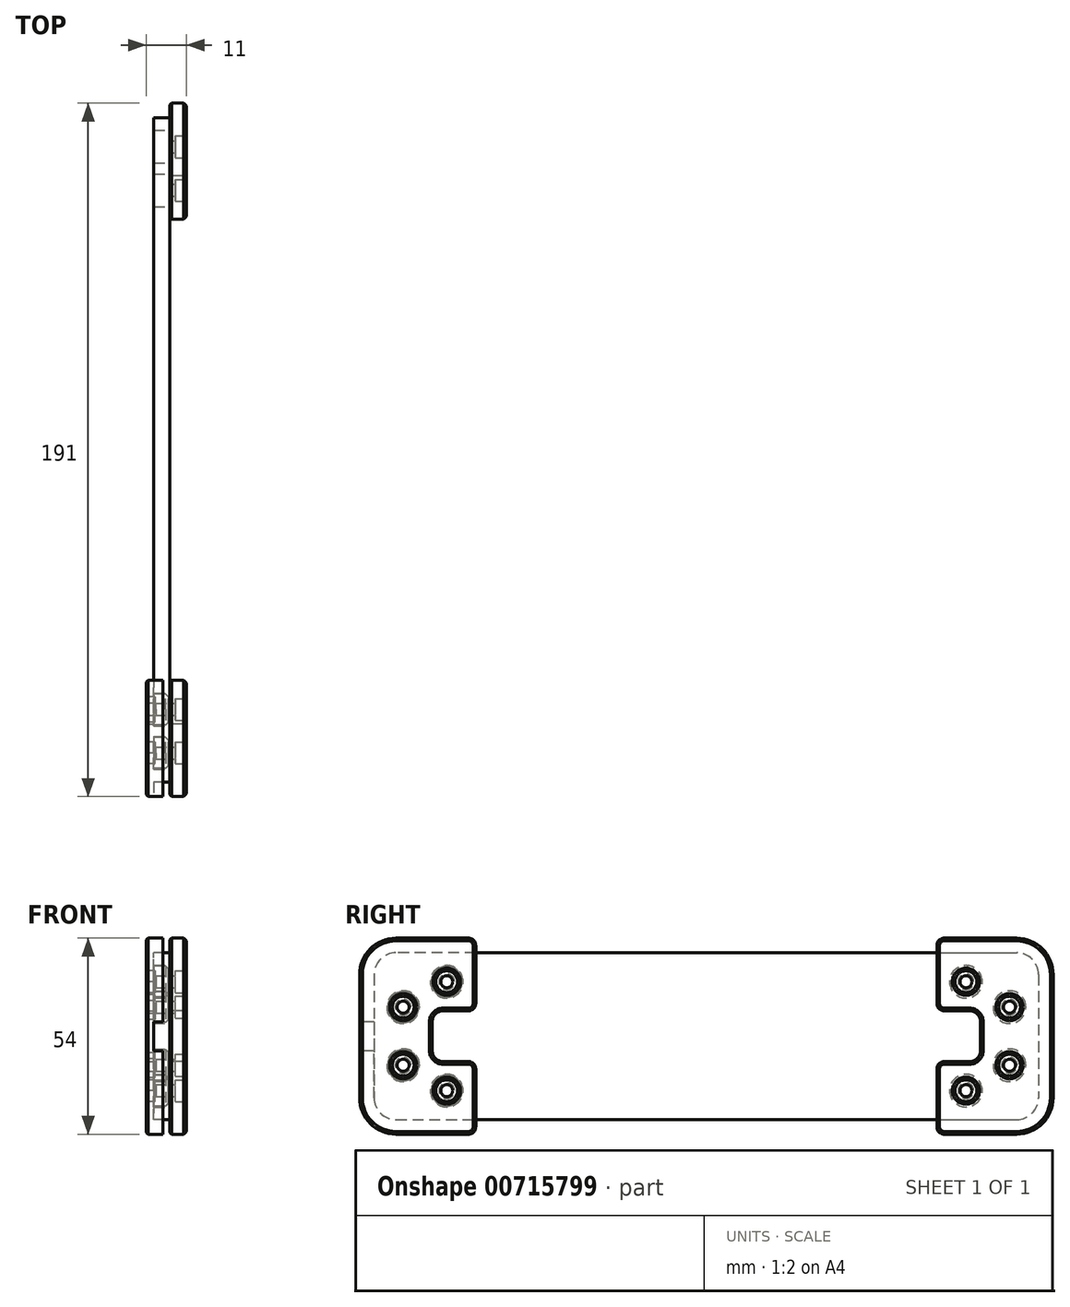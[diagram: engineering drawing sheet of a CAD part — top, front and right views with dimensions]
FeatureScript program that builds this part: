
annotation { "Feature Type Name" : "Feature", "Feature Type Description" : "" }
export const myFeature = defineFeature(function(context is Context, id is Id, definition is map)
    precondition{}
    {
        {
            assignVariable(context, id + "F0", {"name" : "thickness", "anyValue" : 4.5});
        }
        {
            var Q0;
            Q0=qCreatedBy(makeId("Right.planeOp"),FACE);
            var sketch = newSketch(context, id + "F1", { "sketchPlane" : qUnion([Q0])});
            skLineSegment(sketch, "E0.bottom", {"start": v(-85.5, 23) * mm, "end": v(85.5, 23) * mm});
            skLineSegment(sketch, "E0.top", {"start": v(-85.5, -23) * mm, "end": v(85.5, -23) * mm});
            skLineSegment(sketch, "E0.left", {"start": v(-91.5, 17) * mm, "end": v(-91.5, -17) * mm});
            skLineSegment(sketch, "E0.right", {"start": v(91.5, 17) * mm, "end": v(91.5, -17) * mm});
            skPoint(sketch, "E0.middle", {"position": v(0, 0) * mm});
            skPoint(sketch, "E1.visualSharp", {"position": v(-91.5, 23) * mm});
            skArc(sketch, "E1.filletArc", {"start": v(-85.5, 23) * mm, "mid": v(-89.74, 21.24) * mm, "end": v(-91.5, 17) * mm});
            skPoint(sketch, "E2.visualSharp", {"position": v(-91.5, -23) * mm});
            skArc(sketch, "E2.filletArc", {"start": v(-91.5, -17) * mm, "mid": v(-89.74, -21.24) * mm, "end": v(-85.5, -23) * mm});
            skPoint(sketch, "E3.visualSharp", {"position": v(91.5, -23) * mm});
            skArc(sketch, "E3.filletArc", {"start": v(85.5, -23) * mm, "mid": v(89.74, -21.24) * mm, "end": v(91.5, -17) * mm});
            skPoint(sketch, "E4.visualSharp", {"position": v(91.5, 23) * mm});
            skArc(sketch, "E4.filletArc", {"start": v(91.5, 17) * mm, "mid": v(89.74, 21.24) * mm, "end": v(85.5, 23) * mm});
            skSolve(sketch);
        }
        {
            var Q0;
            Q0 = qSketchRegion(id + "F1", true);
            extrude(context, id + "F2", {"entities" : qUnion([Q0]), "endBound" : BoundingType.SYMMETRIC, "depth" : (getVariable(context, 'thickness')) * mm, "offsetDistance" : 25 * mm});
        }
        {
            var Q0;
            Q0=qCreatedBy(makeId("Right.planeOp"),FACE);
            var sketch = newSketch(context, id + "F3", { "sketchPlane" : qUnion([Q0])});
            skCircle(sketch, "E5", {"center": v(-83.5, -8) * mm, "radius": 4.5 * mm});
            skCircle(sketch, "E6", {"center": v(-71.5, -15) * mm, "radius": 4.5 * mm});
            skCircle(sketch, "E7.MirrorC", {"center": v(83.5, -8) * mm, "radius": 4.5 * mm});
            skCircle(sketch, "E8.MirrorC", {"center": v(71.5, -15) * mm, "radius": 4.5 * mm});
            skCircle(sketch, "E9.MirrorC", {"center": v(83.5, 8) * mm, "radius": 4.5 * mm});
            skCircle(sketch, "E10.MirrorC", {"center": v(71.5, 15) * mm, "radius": 4.5 * mm});
            skCircle(sketch, "E11.MirrorC", {"center": v(-71.5, 15) * mm, "radius": 4.5 * mm});
            skCircle(sketch, "E12.MirrorC", {"center": v(-83.5, 8) * mm, "radius": 4.5 * mm});
            skSolve(sketch);
        }
        {
            var Q0;
            Q0 = qSketchRegion(id + "F3", true);
            extrude(context, id + "F4", {"entities" : qUnion([Q0]), "operationType" : NewBodyOperationType.REMOVE, "endBound" : BoundingType.SYMMETRIC, "oppositeDirection" : true, "depth" : 5 * mm, "offsetDistance" : 25 * mm});
        }
        {
            var Q0;
            Q0=makeQuery(id+"F2.opExtrude","CAP_FACE",FACE,{"disambiguationData":[OSD([sQuery(id+"F1.wireOp",EDGE,"E0.bottom"),sQuery(id+"F1.wireOp",EDGE,"E0.top"),sQuery(id+"F1.wireOp",EDGE,"E0.left"),sQuery(id+"F1.wireOp",EDGE,"E0.right"),sQuery(id+"F1.wireOp",EDGE,"E1.filletArc"),sQuery(id+"F1.wireOp",EDGE,"E2.filletArc"),sQuery(id+"F1.wireOp",EDGE,"E3.filletArc"),sQuery(id+"F1.wireOp",EDGE,"E4.filletArc")])],"isStart":false});
            var sketch = newSketch(context, id + "F5", { "sketchPlane" : qUnion([Q0])});
            skLineSegment(sketch, "E13", {"start": v(-75.5, 4) * mm, "end": v(-75.5, -4) * mm});
            skLineSegment(sketch, "E14", {"start": v(-72.5, -7) * mm, "end": v(-63.5, -7) * mm});
            skLineSegment(sketch, "E15", {"start": v(-63.5, -7) * mm, "end": v(-63.5, -27) * mm});
            skLineSegment(sketch, "E16", {"start": v(-63.5, -27) * mm, "end": v(-85.5, -27) * mm});
            skLineSegment(sketch, "E17", {"start": v(-95.5, -17) * mm, "end": v(-95.5, 17) * mm});
            skPoint(sketch, "E18.visualSharp", {"position": v(-75.5, -7) * mm});
            skArc(sketch, "E18.filletArc", {"start": v(-75.5, -4) * mm, "mid": v(-74.62, -6.12) * mm, "end": v(-72.5, -7) * mm});
            skPoint(sketch, "E19.visualSharp", {"position": v(-95.5, -27) * mm});
            skArc(sketch, "E19.filletArc", {"start": v(-95.5, -17) * mm, "mid": v(-92.57, -24.07) * mm, "end": v(-85.5, -27) * mm});
            skLineSegment(sketch, "E20", {"start": v(-83.5, -8) * mm, "end": v(-83.5, 0) * mm, "construction": true});
            skLineSegment(sketch, "E21", {"start": v(-71.5, -15) * mm, "end": v(-63.5, -15) * mm, "construction": true});
            skLineSegment(sketch, "E22", {"start": v(-83.5, -1.98) * mm, "end": v(-75.5, -1.98) * mm, "construction": true});
            skPoint(sketch, "E23.MirrorP", {"position": v(-95.5, 27) * mm});
            skLineSegment(sketch, "E24.MirrorCS", {"start": v(-63.5, 27) * mm, "end": v(-85.5, 27) * mm});
            skLineSegment(sketch, "E25.MirrorCS", {"start": v(-71.5, 15) * mm, "end": v(-63.5, 15) * mm, "construction": true});
            skLineSegment(sketch, "E26.MirrorCS", {"start": v(-83.5, 8) * mm, "end": v(-83.5, 0) * mm, "construction": true});
            skPoint(sketch, "E27.MirrorP", {"position": v(-75.5, 7) * mm});
            skLineSegment(sketch, "E28.MirrorCS", {"start": v(-63.5, 7) * mm, "end": v(-63.5, 27) * mm});
            skLineSegment(sketch, "E29.MirrorCS", {"start": v(-72.5, 7) * mm, "end": v(-63.5, 7) * mm});
            skArc(sketch, "E30.MirrorCS", {"start": v(-75.5, 4) * mm, "mid": v(-74.62, 6.12) * mm, "end": v(-72.5, 7) * mm});
            skArc(sketch, "E31.MirrorCS", {"start": v(-95.5, 17) * mm, "mid": v(-92.57, 24.07) * mm, "end": v(-85.5, 27) * mm});
            skSolve(sketch);
        }
        {
            var Q0;
            Q0 = qSketchRegion(id + "F5", true);
            extrude(context, id + "F6", {"entities" : qUnion([Q0]), "depth" : 4.5 * mm, "offsetDistance" : 25 * mm});
        }
        {
            var Q0;
            Q0=makeQuery(id+"F6.opExtrude","SWEPT_EDGE",EDGE,{"disambiguationData":[OSD([sQuery(id+"F5.wireOp",EDGE,"E17"),sQuery(id+"F5.wireOp",EDGE,"RyQupdBu-5okV-t9er-J7do-R5SVAbqqGuGU")])]});
            var Q1;
            Q1=makeQuery(id+"F6.opExtrude","SWEPT_EDGE",EDGE,{"disambiguationData":[OSD([sQuery(id+"F5.wireOp",EDGE,"E13"),sQuery(id+"F5.wireOp",EDGE,"RyQupdBu-5okV-t9er-J7do-R5SVAbqqGuGU")])]});
            var Q2;
            Q2=makeQuery(id+"F6.opExtrude","SWEPT_EDGE",EDGE,{"disambiguationData":[OSD([sQuery(id+"F5.wireOp",EDGE,"E14"),sQuery(id+"F5.wireOp",EDGE,"E15")])]});
            var Q3;
            Q3=makeQuery(id+"F6.opExtrude","SWEPT_EDGE",EDGE,{"disambiguationData":[OSD([sQuery(id+"F5.wireOp",EDGE,"E15"),sQuery(id+"F5.wireOp",EDGE,"E16")])]});
            var Q4;
            Q4=makeQuery(id+"F6.opExtrude","SWEPT_EDGE",EDGE,{"disambiguationData":[OSD([sQuery(id+"F5.wireOp",EDGE,"E28.MirrorCS"),sQuery(id+"F5.wireOp",EDGE,"E29.MirrorCS")])]});
            var Q5;
            Q5=makeQuery(id+"F6.opExtrude","SWEPT_EDGE",EDGE,{"disambiguationData":[OSD([sQuery(id+"F5.wireOp",EDGE,"E24.MirrorCS"),sQuery(id+"F5.wireOp",EDGE,"E28.MirrorCS")])]});
            fillet(context, id + "F7", {"entities" : qUnion([Q0, Q1, Q2, Q3, Q4, Q5]), "radius" : 2 * mm, "tangentPropagation" : true, "allowEdgeOverflow" : false});
        }
        {
            var Q0;
            Q0=makeQuery(id+"F2.opExtrude","CAP_FACE",FACE,{"disambiguationData":[OSD([sQuery(id+"F1.wireOp",EDGE,"E0.bottom"),sQuery(id+"F1.wireOp",EDGE,"E0.top"),sQuery(id+"F1.wireOp",EDGE,"E0.left"),sQuery(id+"F1.wireOp",EDGE,"E0.right"),sQuery(id+"F1.wireOp",EDGE,"E1.filletArc"),sQuery(id+"F1.wireOp",EDGE,"E2.filletArc"),sQuery(id+"F1.wireOp",EDGE,"E3.filletArc"),sQuery(id+"F1.wireOp",EDGE,"E4.filletArc")])],"isStart":true});
            var sketch = newSketch(context, id + "F8", { "sketchPlane" : qUnion([Q0])});
            skLineSegment(sketch, "E32.0", {"start": v(72.5, -7) * mm, "end": v(63.5, -7) * mm});
            skLineSegment(sketch, "E32.1", {"start": v(75.5, 0) * mm, "end": v(75.5, -4) * mm});
            skLineSegment(sketch, "E32.2", {"start": v(63.5, -27) * mm, "end": v(85.5, -27) * mm});
            skArc(sketch, "E32.3", {"start": v(95.5, -17) * mm, "mid": v(92.57, -24.07) * mm, "end": v(85.5, -27) * mm});
            skLineSegment(sketch, "E32.4", {"start": v(95.5, -17) * mm, "end": v(95.5, 0) * mm});
            skLineSegment(sketch, "E32.5", {"start": v(63.5, -7) * mm, "end": v(63.5, -27) * mm});
            skPoint(sketch, "E33.visualSharp", {"position": v(75.5, -7) * mm});
            skArc(sketch, "E33.filletArc", {"start": v(72.5, -7) * mm, "mid": v(74.62, -6.12) * mm, "end": v(75.5, -4) * mm});
            skArc(sketch, "E34.MirrorCS", {"start": v(72.5, 7) * mm, "mid": v(74.62, 6.12) * mm, "end": v(75.5, 4) * mm});
            skLineSegment(sketch, "E35.MirrorCS", {"start": v(72.5, 7) * mm, "end": v(63.5, 7) * mm});
            skLineSegment(sketch, "E36.MirrorCS", {"start": v(63.5, 27) * mm, "end": v(85.5, 27) * mm});
            skLineSegment(sketch, "E37.MirrorCS", {"start": v(63.5, 7) * mm, "end": v(63.5, 27) * mm});
            skLineSegment(sketch, "E38.MirrorCS", {"start": v(75.5, 0) * mm, "end": v(75.5, 4) * mm});
            skPoint(sketch, "E39.MirrorP", {"position": v(75.5, 7) * mm});
            skArc(sketch, "E40.MirrorCS", {"start": v(95.5, 17) * mm, "mid": v(92.57, 24.07) * mm, "end": v(85.5, 27) * mm});
            skLineSegment(sketch, "E41.MirrorCS", {"start": v(95.5, 17) * mm, "end": v(95.5, 0) * mm});
            skSolve(sketch);
        }
        {
            var Q0;
            Q0 = qSketchRegion(id + "F8", true);
            extrude(context, id + "F9", {"entities" : qUnion([Q0]), "depth" : 2 * mm, "offsetDistance" : 25 * mm});
        }
        {
            var Q0;
            Q0=makeQuery(id+"F9.opExtrude","CAP_FACE",FACE,{"disambiguationData":[OSD([sQuery(id+"F8.wireOp",EDGE,"E32.0"),sQuery(id+"F8.wireOp",EDGE,"E32.1"),sQuery(id+"F8.wireOp",EDGE,"E32.2"),sQuery(id+"F8.wireOp",EDGE,"E32.3"),sQuery(id+"F8.wireOp",EDGE,"E32.4"),sQuery(id+"F8.wireOp",EDGE,"E32.5"),sQuery(id+"F8.wireOp",EDGE,"E32.6"),sQuery(id+"F8.wireOp",EDGE,"E33.filletArc")])],"isStart":true});
            var sketch = newSketch(context, id + "F10", { "sketchPlane" : qUnion([Q0])});
            skLineSegment(sketch, "E42", {"start": v(-95.5, -4) * mm, "end": v(-95.5, -17) * mm});
            skLineSegment(sketch, "E43", {"start": v(-85.5, -27) * mm, "end": v(-63.5, -27) * mm});
            skLineSegment(sketch, "E44", {"start": v(-63.5, -27) * mm, "end": v(-63.5, -23) * mm});
            skLineSegment(sketch, "E45", {"start": v(-63.5, -23) * mm, "end": v(-85.5, -23) * mm});
            skLineSegment(sketch, "E46", {"start": v(-91.5, -17) * mm, "end": v(-91.5, -4) * mm});
            skLineSegment(sketch, "E47", {"start": v(-91.5, -4) * mm, "end": v(-95.5, -4) * mm});
            skPoint(sketch, "E48.visualSharp", {"position": v(-91.5, -23) * mm});
            skArc(sketch, "E48.filletArc", {"start": v(-91.5, -17) * mm, "mid": v(-89.74, -21.24) * mm, "end": v(-85.5, -23) * mm});
            skPoint(sketch, "E49.visualSharp", {"position": v(-95.5, -27) * mm});
            skArc(sketch, "E49.filletArc", {"start": v(-95.5, -17) * mm, "mid": v(-92.57, -24.07) * mm, "end": v(-85.5, -27) * mm});
            skLineSegment(sketch, "E50.MirrorCS", {"start": v(-85.5, 27) * mm, "end": v(-63.5, 27) * mm});
            skPoint(sketch, "E51.MirrorP", {"position": v(-95.5, 27) * mm});
            skLineSegment(sketch, "E52.MirrorCS", {"start": v(-91.5, 17) * mm, "end": v(-91.5, 4) * mm});
            skPoint(sketch, "E53.MirrorP", {"position": v(-91.5, 23) * mm});
            skArc(sketch, "E54.MirrorCS", {"start": v(-95.5, 17) * mm, "mid": v(-92.57, 24.07) * mm, "end": v(-85.5, 27) * mm});
            skLineSegment(sketch, "E55.MirrorCS", {"start": v(-95.5, 4) * mm, "end": v(-95.5, 17) * mm});
            skLineSegment(sketch, "E56.MirrorCS", {"start": v(-91.5, 4) * mm, "end": v(-95.5, 4) * mm});
            skLineSegment(sketch, "E57.MirrorCS", {"start": v(-63.5, 23) * mm, "end": v(-85.5, 23) * mm});
            skLineSegment(sketch, "E58.MirrorCS", {"start": v(-63.5, 27) * mm, "end": v(-63.5, 23) * mm});
            skArc(sketch, "E59.MirrorCS", {"start": v(-91.5, 17) * mm, "mid": v(-89.74, 21.24) * mm, "end": v(-85.5, 23) * mm});
            skSolve(sketch);
        }
        {
            var Q0;
            Q0 = qSketchRegion(id + "F10", true);
            extrude(context, id + "F11", {"entities" : qUnion([Q0]), "operationType" : NewBodyOperationType.ADD, "depth" : 2.5 * mm, "offsetDistance" : 25 * mm});
        }
        {
            var Q0;
            Q0=makeQuery(id+"F9.opExtrude","SWEPT_EDGE",EDGE,{"disambiguationData":[OSD([sQuery(id+"F8.wireOp",EDGE,"E32.2"),sQuery(id+"F8.wireOp",EDGE,"E32.5")])]});
            var Q1;
            Q1=makeQuery(id+"F9.opExtrude","SWEPT_EDGE",EDGE,{"disambiguationData":[OSD([sQuery(id+"F8.wireOp",EDGE,"E32.0"),sQuery(id+"F8.wireOp",EDGE,"E32.5")])]});
            var Q2;
            Q2=makeQuery(id+"F9.opExtrude","SWEPT_EDGE",EDGE,{"disambiguationData":[OSD([sQuery(id+"F8.wireOp",EDGE,"E32.1"),sQuery(id+"F8.wireOp",EDGE,"E32.6")])]});
            var Q3;
            Q3=makeQuery(id+"F9.opExtrude","SWEPT_EDGE",EDGE,{"disambiguationData":[OSD([sQuery(id+"F8.wireOp",EDGE,"E32.4"),sQuery(id+"F8.wireOp",EDGE,"E32.6")])]});
            var Q4;
            Q4=makeQuery(id+"F11.boolean.opBoolean","MERGE",EDGE,{"derivedFrom":[makeQuery(id+"F9.opExtrude","SWEPT_EDGE",EDGE,{"disambiguationData":[OSD([sQuery(id+"F8.wireOp",EDGE,"E36.MirrorCS"),sQuery(id+"F8.wireOp",EDGE,"E37.MirrorCS")])]}),makeQuery(id+"F11.opExtrude","SWEPT_EDGE",EDGE,{"disambiguationData":[OSD([sQuery(id+"F10.wireOp",EDGE,"E50.MirrorCS"),sQuery(id+"F10.wireOp",EDGE,"E58.MirrorCS")])]})]});
            var Q5;
            Q5=makeQuery(id+"F9.opExtrude","SWEPT_EDGE",EDGE,{"disambiguationData":[OSD([sQuery(id+"F8.wireOp",EDGE,"E35.MirrorCS"),sQuery(id+"F8.wireOp",EDGE,"E37.MirrorCS")])]});
            fillet(context, id + "F12", {"entities" : qUnion([Q0, Q1, Q2, Q3, Q4, Q5]), "radius" : 2 * mm, "tangentPropagation" : true, "allowEdgeOverflow" : false});
        }
        {
            var Q0;
            Q0=makeQuery(id+"F9.opExtrude","CAP_FACE",FACE,{"disambiguationData":[OSD([sQuery(id+"F8.wireOp",EDGE,"E32.0"),sQuery(id+"F8.wireOp",EDGE,"E32.1"),sQuery(id+"F8.wireOp",EDGE,"E32.2"),sQuery(id+"F8.wireOp",EDGE,"E32.3"),sQuery(id+"F8.wireOp",EDGE,"E32.4"),sQuery(id+"F8.wireOp",EDGE,"E32.5"),sQuery(id+"F8.wireOp",EDGE,"E32.6"),sQuery(id+"F8.wireOp",EDGE,"E33.filletArc")])],"isStart":true});
            var sketch = newSketch(context, id + "F13", { "sketchPlane" : qUnion([Q0])});
            skCircle(sketch, "E60", {"center": v(-71.5, -15) * mm, "radius": 4.25 * mm});
            skCircle(sketch, "E61", {"center": v(-83.5, -8) * mm, "radius": 4.25 * mm});
            skCircle(sketch, "E62.MirrorC", {"center": v(-83.5, 8) * mm, "radius": 4.25 * mm});
            skCircle(sketch, "E63.MirrorC", {"center": v(-71.5, 15) * mm, "radius": 4.25 * mm});
            skSolve(sketch);
        }
        {
            var Q0;
            Q0 = qSketchRegion(id + "F13", true);
            extrude(context, id + "F14", {"entities" : qUnion([Q0]), "operationType" : NewBodyOperationType.ADD, "depth" : 4 * mm, "offsetDistance" : 25 * mm});
        }
        {
            var Q0;
            Q0=makeQuery(id+"F14.opExtrude","CAP_FACE",FACE,{"disambiguationData":[OSD([sQuery(id+"F13.wireOp",EDGE,"E61")])],"isStart":false});
            var sketch = newSketch(context, id + "F15", { "sketchPlane" : qUnion([Q0])});
            skCircle(sketch, "E64", {"center": v(-71.5, -15) * mm, "radius": 1.65 * mm});
            skCircle(sketch, "E65", {"center": v(-83.5, -8) * mm, "radius": 1.65 * mm});
            skCircle(sketch, "E66.MirrorC", {"center": v(-71.5, 15) * mm, "radius": 1.65 * mm});
            skCircle(sketch, "E67.MirrorC", {"center": v(-83.5, 8) * mm, "radius": 1.65 * mm});
            skSolve(sketch);
        }
        {
            var Q0;
            Q0 = qSketchRegion(id + "F15", true);
            extrude(context, id + "F16", {"entities" : qUnion([Q0]), "operationType" : NewBodyOperationType.REMOVE, "endBound" : BoundingType.THROUGH_ALL, "oppositeDirection" : true, "depth" : 25 * mm, "offsetDistance" : 25 * mm});
        }
        {
            var Q0;
            Q0=makeQuery(id+"F9.opExtrude","CAP_FACE",FACE,{"disambiguationData":[OSD([sQuery(id+"F8.wireOp",EDGE,"E32.0"),sQuery(id+"F8.wireOp",EDGE,"E32.1"),sQuery(id+"F8.wireOp",EDGE,"E32.2"),sQuery(id+"F8.wireOp",EDGE,"E32.3"),sQuery(id+"F8.wireOp",EDGE,"E32.4"),sQuery(id+"F8.wireOp",EDGE,"E32.5"),sQuery(id+"F8.wireOp",EDGE,"E32.6"),sQuery(id+"F8.wireOp",EDGE,"E33.filletArc")])],"isStart":false});
            var sketch = newSketch(context, id + "F17", { "sketchPlane" : qUnion([Q0])});
            skCircle(sketch, "E68.cCircle", {"center": v(71.5, -15) * mm, "radius": 3.46 * mm, "construction": true});
            skLineSegment(sketch, "E68.0", {"start": v(69.77, -12) * mm, "end": v(73.23, -12) * mm});
            skLineSegment(sketch, "E68.1", {"start": v(73.23, -12) * mm, "end": v(74.96, -15) * mm});
            skLineSegment(sketch, "E68.2", {"start": v(74.96, -15) * mm, "end": v(73.23, -18) * mm});
            skLineSegment(sketch, "E68.3", {"start": v(73.23, -18) * mm, "end": v(69.77, -18) * mm});
            skLineSegment(sketch, "E68.4", {"start": v(69.77, -18) * mm, "end": v(68.04, -15) * mm});
            skLineSegment(sketch, "E68.5", {"start": v(68.04, -15) * mm, "end": v(69.77, -12) * mm});
            skCircle(sketch, "E69.cCircle", {"center": v(83.5, -8) * mm, "radius": 3.46 * mm, "construction": true});
            skLineSegment(sketch, "E69.0", {"start": v(80.5, -6.27) * mm, "end": v(83.5, -4.54) * mm});
            skLineSegment(sketch, "E69.1", {"start": v(83.5, -4.54) * mm, "end": v(86.5, -6.27) * mm});
            skLineSegment(sketch, "E69.2", {"start": v(86.5, -6.27) * mm, "end": v(86.5, -9.73) * mm});
            skLineSegment(sketch, "E69.3", {"start": v(86.5, -9.73) * mm, "end": v(83.5, -11.46) * mm});
            skLineSegment(sketch, "E69.4", {"start": v(83.5, -11.46) * mm, "end": v(80.5, -9.73) * mm});
            skLineSegment(sketch, "E69.5", {"start": v(80.5, -9.73) * mm, "end": v(80.5, -6.27) * mm});
            skLineSegment(sketch, "E70.MirrorCS", {"start": v(68.04, 15) * mm, "end": v(69.77, 12) * mm});
            skLineSegment(sketch, "E71.MirrorCS", {"start": v(69.77, 18) * mm, "end": v(68.04, 15) * mm});
            skLineSegment(sketch, "E72.MirrorCS", {"start": v(69.77, 12) * mm, "end": v(73.23, 12) * mm});
            skLineSegment(sketch, "E73.MirrorCS", {"start": v(74.96, 15) * mm, "end": v(73.23, 18) * mm});
            skLineSegment(sketch, "E74.MirrorCS", {"start": v(73.23, 18) * mm, "end": v(69.77, 18) * mm});
            skLineSegment(sketch, "E75.MirrorCS", {"start": v(73.23, 12) * mm, "end": v(74.96, 15) * mm});
            skLineSegment(sketch, "E76.MirrorCS", {"start": v(83.5, 4.54) * mm, "end": v(86.5, 6.27) * mm});
            skLineSegment(sketch, "E77.MirrorCS", {"start": v(86.5, 9.73) * mm, "end": v(83.5, 11.46) * mm});
            skCircle(sketch, "E78.MirrorC", {"center": v(71.5, 15) * mm, "radius": 3.46 * mm, "construction": true});
            skLineSegment(sketch, "E79.MirrorCS", {"start": v(86.5, 6.27) * mm, "end": v(86.5, 9.73) * mm});
            skCircle(sketch, "E80.MirrorC", {"center": v(83.5, 8) * mm, "radius": 3.46 * mm, "construction": true});
            skLineSegment(sketch, "E81.MirrorCS", {"start": v(80.5, 9.73) * mm, "end": v(80.5, 6.27) * mm});
            skLineSegment(sketch, "E82.MirrorCS", {"start": v(80.5, 6.27) * mm, "end": v(83.5, 4.54) * mm});
            skLineSegment(sketch, "E83.MirrorCS", {"start": v(83.5, 11.46) * mm, "end": v(80.5, 9.73) * mm});
            skSolve(sketch);
        }
        {
            var Q0;
            Q0 = qSketchRegion(id + "F17", true);
            extrude(context, id + "F18", {"entities" : qUnion([Q0]), "operationType" : NewBodyOperationType.REMOVE, "oppositeDirection" : true, "depth" : 2.4 * mm, "offsetDistance" : 25 * mm});
        }
        {
            var Q0;
            Q0=makeQuery(id+"F14.opExtrude","CAP_EDGE",EDGE,{"disambiguationData":[OSD([sQuery(id+"F13.wireOp",EDGE,"99nuNubE-fCBx-eOUg-4Eev-Zh7OqMbQXb6X")])],"isStart":false});
            var Q1;
            Q1=makeQuery(id+"F14.opExtrude","CAP_EDGE",EDGE,{"disambiguationData":[OSD([sQuery(id+"F13.wireOp",EDGE,"E60")])],"isStart":false});
            var Q2;
            Q2=makeQuery(id+"F14.opExtrude","CAP_EDGE",EDGE,{"disambiguationData":[OSD([sQuery(id+"F13.wireOp",EDGE,"E61")])],"isStart":false});
            var Q3;
            Q3=makeQuery(id+"F14.opExtrude","CAP_EDGE",EDGE,{"disambiguationData":[OSD([sQuery(id+"F13.wireOp",EDGE,"E62.MirrorC")])],"isStart":false});
            var Q4;
            Q4=makeQuery(id+"F14.opExtrude","CAP_EDGE",EDGE,{"disambiguationData":[OSD([sQuery(id+"F13.wireOp",EDGE,"E63.MirrorC")])],"isStart":false});
            chamfer(context, id + "F19", {"entities" : qUnion([Q0, Q1, Q2, Q3, Q4]), "width" : .75 * mm, "tangentPropagation" : true});
        }
        {
            var Q0;
            Q0=makeQuery(id+"F9.opExtrude","CAP_FACE",FACE,{"disambiguationData":[OSD([sQuery(id+"F8.wireOp",EDGE,"E32.0"),sQuery(id+"F8.wireOp",EDGE,"E32.1"),sQuery(id+"F8.wireOp",EDGE,"E32.2"),sQuery(id+"F8.wireOp",EDGE,"E32.3"),sQuery(id+"F8.wireOp",EDGE,"E32.4"),sQuery(id+"F8.wireOp",EDGE,"E32.5"),sQuery(id+"F8.wireOp",EDGE,"E32.6"),sQuery(id+"F8.wireOp",EDGE,"E33.filletArc")])],"isStart":false});
            chamfer(context, id + "F20", {"entities" : qUnion([Q0]), "width" : .5 * mm, "tangentPropagation" : true});
        }
        {
            var Q0;
            Q0=makeQuery(id+"F6.opExtrude","CAP_FACE",FACE,{"disambiguationData":[OSD([sQuery(id+"F5.wireOp",EDGE,"E13"),sQuery(id+"F5.wireOp",EDGE,"E14"),sQuery(id+"F5.wireOp",EDGE,"E15"),sQuery(id+"F5.wireOp",EDGE,"E16"),sQuery(id+"F5.wireOp",EDGE,"E17"),sQuery(id+"F5.wireOp",EDGE,"RyQupdBu-5okV-t9er-J7do-R5SVAbqqGuGU"),sQuery(id+"F5.wireOp",EDGE,"E18.filletArc"),sQuery(id+"F5.wireOp",EDGE,"E19.filletArc")])],"isStart":false});
            var sketch = newSketch(context, id + "F21", { "sketchPlane" : qUnion([Q0])});
            skCircle(sketch, "E84", {"center": v(-71.5, -15) * mm, "radius": 3 * mm});
            skCircle(sketch, "E85", {"center": v(-83.5, -8) * mm, "radius": 3 * mm});
            skCircle(sketch, "E86.MirrorC", {"center": v(-83.5, 8) * mm, "radius": 3 * mm});
            skCircle(sketch, "E87.MirrorC", {"center": v(-71.5, 15) * mm, "radius": 3 * mm});
            skSolve(sketch);
        }
        {
            var Q0;
            Q0 = qSketchRegion(id + "F21", true);
            extrude(context, id + "F22", {"entities" : qUnion([Q0]), "operationType" : NewBodyOperationType.REMOVE, "oppositeDirection" : true, "depth" : 3 * mm, "offsetDistance" : 25 * mm});
        }
        {
            var Q0;
            Q0=makeQuery(id+"F22.boolean.opBoolean","COPY",FACE,{"derivedFrom":makeQuery(id+"F22.opExtrude","CAP_FACE",FACE,{"disambiguationData":[OSD([sQuery(id+"F21.wireOp",EDGE,"E85")])],"isStart":false})});
            var sketch = newSketch(context, id + "F23", { "sketchPlane" : qUnion([Q0])});
            skCircle(sketch, "E88", {"center": v(-83.5, -8) * mm, "radius": 1.65 * mm});
            skCircle(sketch, "E89", {"center": v(-71.5, -15) * mm, "radius": 1.65 * mm});
            skCircle(sketch, "E90.MirrorC", {"center": v(-71.5, 15) * mm, "radius": 1.65 * mm});
            skCircle(sketch, "E91.MirrorC", {"center": v(-83.5, 8) * mm, "radius": 1.65 * mm});
            skSolve(sketch);
        }
        {
            var Q0;
            Q0 = qSketchRegion(id + "F23", true);
            extrude(context, id + "F24", {"entities" : qUnion([Q0]), "operationType" : NewBodyOperationType.REMOVE, "endBound" : BoundingType.THROUGH_ALL, "oppositeDirection" : true, "depth" : 25 * mm, "offsetDistance" : 25 * mm});
        }
        {
            var Q0;
            Q0=makeQuery(id+"F6.opExtrude","CAP_FACE",FACE,{"disambiguationData":[OSD([sQuery(id+"F5.wireOp",EDGE,"E13"),sQuery(id+"F5.wireOp",EDGE,"E14"),sQuery(id+"F5.wireOp",EDGE,"E15"),sQuery(id+"F5.wireOp",EDGE,"E16"),sQuery(id+"F5.wireOp",EDGE,"E17"),sQuery(id+"F5.wireOp",EDGE,"RyQupdBu-5okV-t9er-J7do-R5SVAbqqGuGU"),sQuery(id+"F5.wireOp",EDGE,"E18.filletArc"),sQuery(id+"F5.wireOp",EDGE,"E19.filletArc")])],"isStart":false});
            chamfer(context, id + "F25", {"entities" : qUnion([Q0]), "width" : .75 * mm, "tangentPropagation" : true});
        }
        {
            var Q0;
            Q0=makeQuery(id+"F6.opExtrude","CAP_FACE",FACE,{"disambiguationData":[OSD([sQuery(id+"F5.wireOp",EDGE,"E13"),sQuery(id+"F5.wireOp",EDGE,"E14"),sQuery(id+"F5.wireOp",EDGE,"E15"),sQuery(id+"F5.wireOp",EDGE,"E16"),sQuery(id+"F5.wireOp",EDGE,"E17"),sQuery(id+"F5.wireOp",EDGE,"RyQupdBu-5okV-t9er-J7do-R5SVAbqqGuGU"),sQuery(id+"F5.wireOp",EDGE,"E18.filletArc"),sQuery(id+"F5.wireOp",EDGE,"E19.filletArc")])],"isStart":true});
            chamfer(context, id + "F26", {"entities" : qUnion([Q0]), "width" : .5 * mm, "tangentPropagation" : true});
        }
        {
            var Q0;
            Q0=makeQuery(id+"F18.boolean.opBoolean","COPY",FACE,{"derivedFrom":makeQuery(id+"F18.opExtrude","CAP_FACE",FACE,{"disambiguationData":[OSD([sQuery(id+"F17.wireOp",EDGE,"E69.0"),sQuery(id+"F17.wireOp",EDGE,"E69.1"),sQuery(id+"F17.wireOp",EDGE,"E69.2"),sQuery(id+"F17.wireOp",EDGE,"E69.3"),sQuery(id+"F17.wireOp",EDGE,"E69.4"),sQuery(id+"F17.wireOp",EDGE,"E69.5")])],"isStart":false})});
            var sketch = newSketch(context, id + "F27", { "sketchPlane" : qUnion([Q0])});
            skCircle(sketch, "E92", {"center": v(71.5, 15) * mm, "radius": 1.65 * mm});
            skCircle(sketch, "E93", {"center": v(83.5, 8) * mm, "radius": 1.65 * mm});
            skCircle(sketch, "E94", {"center": v(83.5, -8) * mm, "radius": 1.65 * mm});
            skCircle(sketch, "E95", {"center": v(71.5, -15) * mm, "radius": 1.65 * mm});
            skSolve(sketch);
        }
        {
            var Q0;
            Q0 = qSketchRegion(id + "F27", true);
            extrude(context, id + "F28", {"entities" : qUnion([Q0]), "operationType" : NewBodyOperationType.ADD, "oppositeDirection" : true, "depth" : .2 * mm, "offsetDistance" : 25 * mm});
        }
        {
            var Q0;
            Q0=makeQuery(id+"F6.opExtrude","SWEPT_BODY",BODY,{"disambiguationData":[OSD([sQuery(id+"F5.wireOp",EDGE,"E13"),sQuery(id+"F5.wireOp",EDGE,"E14"),sQuery(id+"F5.wireOp",EDGE,"E15"),sQuery(id+"F5.wireOp",EDGE,"E16"),sQuery(id+"F5.wireOp",EDGE,"E17"),sQuery(id+"F5.wireOp",EDGE,"RyQupdBu-5okV-t9er-J7do-R5SVAbqqGuGU"),sQuery(id+"F5.wireOp",EDGE,"E18.filletArc"),sQuery(id+"F5.wireOp",EDGE,"E19.filletArc")])]});
            var Q1;
            Q1=makeQuery(id+"F9.opExtrude","SWEPT_BODY",BODY,{"disambiguationData":[OSD([sQuery(id+"F8.wireOp",EDGE,"E32.0"),sQuery(id+"F8.wireOp",EDGE,"E32.1"),sQuery(id+"F8.wireOp",EDGE,"E32.2"),sQuery(id+"F8.wireOp",EDGE,"E32.3"),sQuery(id+"F8.wireOp",EDGE,"E32.4"),sQuery(id+"F8.wireOp",EDGE,"E32.5"),sQuery(id+"F8.wireOp",EDGE,"E32.6"),sQuery(id+"F8.wireOp",EDGE,"E33.filletArc")])]});
            var Q2;
            Q2=makeQuery(id+"F8eMJDgGYNtHPyV_3.opPattern","COPY",BODY,{"derivedFrom":makeQuery(id+"F6.opExtrude","SWEPT_BODY",BODY,{"disambiguationData":[OSD([sQuery(id+"F5.wireOp",EDGE,"E13"),sQuery(id+"F5.wireOp",EDGE,"E14"),sQuery(id+"F5.wireOp",EDGE,"E15"),sQuery(id+"F5.wireOp",EDGE,"E16"),sQuery(id+"F5.wireOp",EDGE,"E17"),sQuery(id+"F5.wireOp",EDGE,"RyQupdBu-5okV-t9er-J7do-R5SVAbqqGuGU"),sQuery(id+"F5.wireOp",EDGE,"E18.filletArc"),sQuery(id+"F5.wireOp",EDGE,"E19.filletArc")])]}),"instanceName":"1"});
            var Q3;
            Q3=makeQuery(id+"F8eMJDgGYNtHPyV_3.opPattern","COPY",BODY,{"derivedFrom":makeQuery(id+"F9.opExtrude","SWEPT_BODY",BODY,{"disambiguationData":[OSD([sQuery(id+"F8.wireOp",EDGE,"E32.0"),sQuery(id+"F8.wireOp",EDGE,"E32.1"),sQuery(id+"F8.wireOp",EDGE,"E32.2"),sQuery(id+"F8.wireOp",EDGE,"E32.3"),sQuery(id+"F8.wireOp",EDGE,"E32.4"),sQuery(id+"F8.wireOp",EDGE,"E32.5"),sQuery(id+"F8.wireOp",EDGE,"E32.6"),sQuery(id+"F8.wireOp",EDGE,"E33.filletArc")])]}),"instanceName":"1"});
            var Q4;
            Q4=qCreatedBy(makeId("Front.planeOp"),FACE);
            mirror(context, id + "F29", {"entities" : qUnion([Q0, Q1, Q2, Q3]), "mirrorPlane" : qUnion([Q4])});
        }
    });
